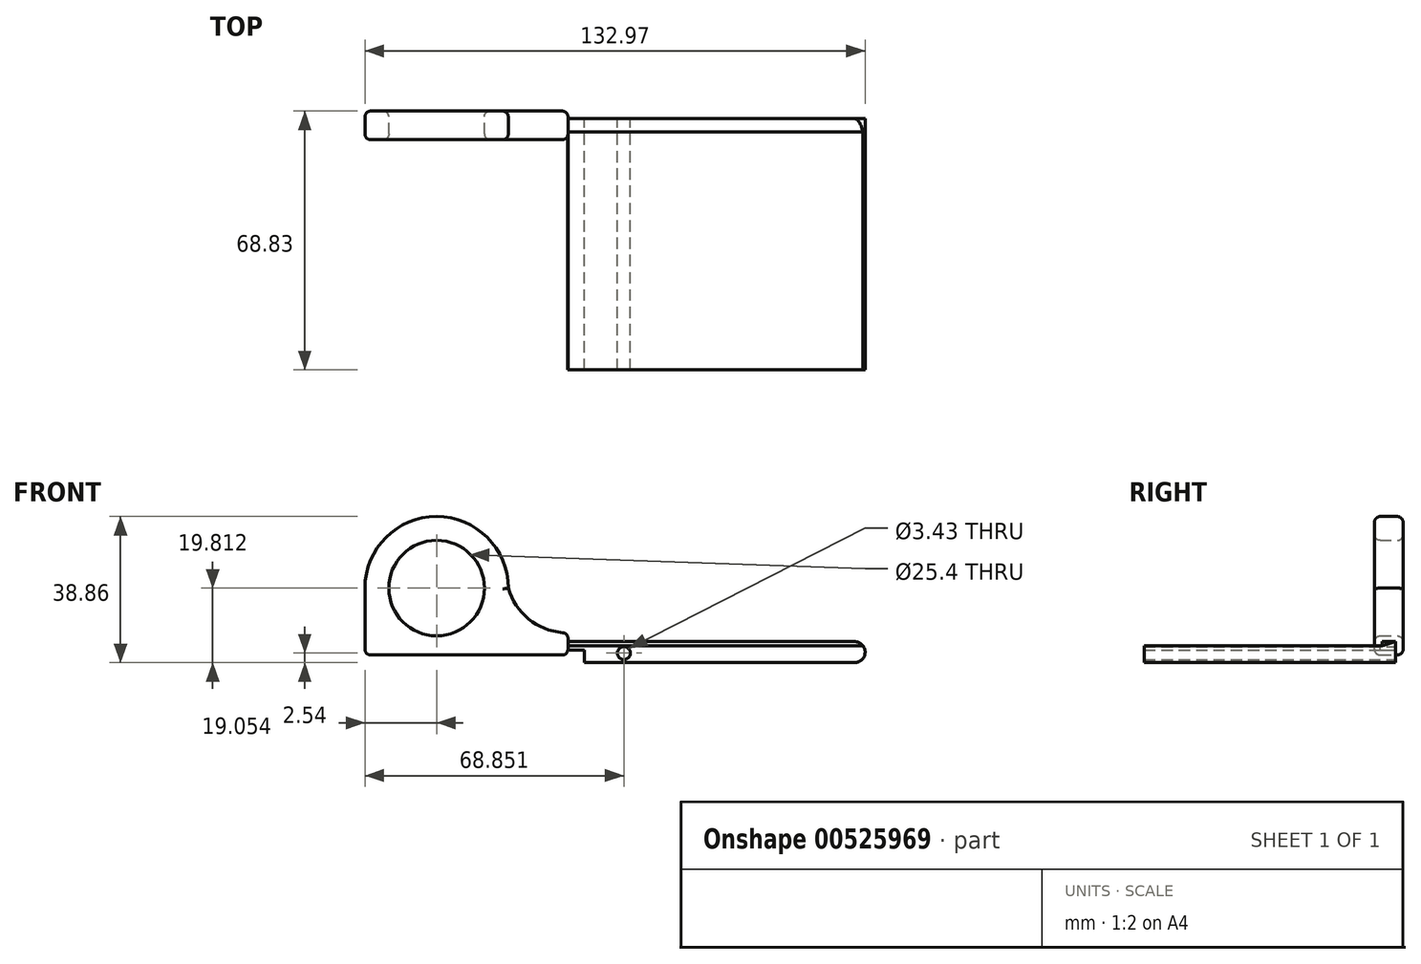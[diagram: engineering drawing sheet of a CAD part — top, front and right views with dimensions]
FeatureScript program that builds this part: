
annotation { "Feature Type Name" : "Feature", "Feature Type Description" : "" }
export const myFeature = defineFeature(function(context is Context, id is Id, definition is map)
    precondition{}
    {
        {
            var Q0;
            Q0=qCreatedBy(makeId("Front.planeOp"),FACE);
            var sketch = newSketch(context, id + "F0", { "sketchPlane" : qUnion([Q0])});
            skLineSegment(sketch, "E0", {"start": v(-53.86, -34.26) * mm, "end": v(-53.86, -16.48) * mm});
            skLineSegment(sketch, "E1", {"start": v(-53.86, -34.26) * mm, "end": v(0.12, -34.26) * mm});
            skLineSegment(sketch, "E2", {"start": v(0.12, -34.26) * mm, "end": v(0.12, -28.4) * mm});
            skLineSegment(sketch, "E3", {"start": v(0.12, -30.7) * mm, "end": v(76.32, -30.7) * mm});
            skArc(sketch, "E4", {"start": v(-15.76, -16.48) * mm, "mid": v(-34.8, 2.57) * mm, "end": v(-53.86, -16.48) * mm});
            skArc(sketch, "E5", {"start": v(-15.76, -16.48) * mm, "mid": v(-9.8, -25.09) * mm, "end": v(0.12, -28.4) * mm});
            skCircle(sketch, "E6", {"center": v(-34.8, -16.48) * mm, "radius": 12.7 * mm});
            skLineSegment(sketch, "E7", {"start": v(4.44, -32.99) * mm, "end": v(0.12, -32.99) * mm});
            skArc(sketch, "E8", {"start": v(76.32, -36.29) * mm, "mid": v(79.11, -33.5) * mm, "end": v(76.32, -30.7) * mm});
            skLineSegment(sketch, "E9", {"start": v(76.32, -36.29) * mm, "end": v(4.45, -36.29) * mm});
            skLineSegment(sketch, "E10", {"start": v(4.45, -36.29) * mm, "end": v(4.44, -32.99) * mm});
            skCircle(sketch, "E11", {"center": v(15, -33.75) * mm, "radius": 1.71 * mm});
            skSolve(sketch);
        }
        {
            var Q0;
            Q0=makeQuery(id+"F0.imprint","IMPRINT",FACE,{"disambiguationData":[TD([[makeQuery(id+"F0.imprint","IMPRINT",EDGE,{"derivedFrom":sQuery(id+"F0.wireOp",EDGE,"E0")}),-1.0]])]});
            extrude(context, id + "F1", {"entities" : qUnion([Q0]), "endBound" : BoundingType.SYMMETRIC, "depth" : 7.62 * mm});
        }
        {
            var Q0;
            {var subQ1=sQuery(id+"F0.wireOp",EDGE,"E3");Q0=makeQuery(id+"F0.imprint","IMPRINT",FACE,{"disambiguationData":[TD([[makeQuery(id+"F0.imprint","IMPRINT",EDGE,{"derivedFrom":subQ1}),-1.0]])]});}
            extrude(context, id + "F2", {"entities" : qUnion([Q0]), "operationType" : NewBodyOperationType.ADD, "endBound" : BoundingType.SYMMETRIC, "depth" : 3.56 * mm});
        }
        {
            var Q0;
            Q0=makeQuery(id+"F1.opExtrude","CAP_EDGE",EDGE,{"disambiguationData":[OSD([sQuery(id+"F0.wireOp",EDGE,"E6")])],"isStart":false});
            var Q1;
            Q1=makeQuery(id+"F1.opExtrude","CAP_EDGE",EDGE,{"disambiguationData":[OSD([sQuery(id+"F0.wireOp",EDGE,"E6")])],"isStart":true});
            var Q2;
            Q2=makeQuery(id+"F1.opExtrude","CAP_EDGE",EDGE,{"disambiguationData":[OSD([sQuery(id+"F0.wireOp",EDGE,"E0")])],"isStart":true});
            var Q3;
            Q3=makeQuery(id+"F1.opExtrude","CAP_EDGE",EDGE,{"disambiguationData":[OSD([sQuery(id+"F0.wireOp",EDGE,"E0")])],"isStart":false});
            var Q4;
            Q4=makeQuery(id+"F1.opExtrude","SWEPT_EDGE",EDGE,{"disambiguationData":[OSD([sQuery(id+"F0.wireOp",EDGE,"E0"),sQuery(id+"F0.wireOp",EDGE,"E1")])]});
            var Q5;
            Q5=makeQuery(id+"F1.opExtrude","CAP_EDGE",EDGE,{"disambiguationData":[OSD([sQuery(id+"F0.wireOp",EDGE,"E1")])],"isStart":false});
            var Q6;
            Q6=makeQuery(id+"F1.opExtrude","CAP_EDGE",EDGE,{"disambiguationData":[OSD([sQuery(id+"F0.wireOp",EDGE,"E1")])],"isStart":true});
            var Q7;
            Q7=makeQuery(id+"F1.opExtrude","CAP_EDGE",EDGE,{"disambiguationData":[OSD([sQuery(id+"F0.wireOp",EDGE,"E4")])],"isStart":false});
            var Q8;
            Q8=makeQuery(id+"F1.opExtrude","CAP_EDGE",EDGE,{"disambiguationData":[OSD([sQuery(id+"F0.wireOp",EDGE,"E4")])],"isStart":true});
            var Q9;
            Q9=makeQuery(id+"F1.opExtrude","CAP_EDGE",EDGE,{"disambiguationData":[OSD([sQuery(id+"F0.wireOp",EDGE,"E5")])],"isStart":true});
            var Q10;
            Q10=makeQuery(id+"F1.opExtrude","CAP_EDGE",EDGE,{"disambiguationData":[OSD([sQuery(id+"F0.wireOp",EDGE,"E5")])],"isStart":false});
            var Q11;
            Q11=makeQuery(id+"F1.opExtrude","CAP_EDGE",EDGE,{"disambiguationData":[OSD([sQuery(id+"F0.wireOp",EDGE,"E2")])],"isStart":false});
            var Q12;
            Q12=makeQuery(id+"F1.opExtrude","SWEPT_EDGE",EDGE,{"disambiguationData":[OSD([sQuery(id+"F0.wireOp",EDGE,"E2"),sQuery(id+"F0.wireOp",EDGE,"E5")])]});
            var Q13;
            Q13=makeQuery(id+"F1.opExtrude","CAP_EDGE",EDGE,{"disambiguationData":[OSD([sQuery(id+"F0.wireOp",EDGE,"E2")])],"isStart":true});
            var Q14;
            Q14=makeQuery(id+"F1.opExtrude","SWEPT_EDGE",EDGE,{"disambiguationData":[OSD([sQuery(id+"F0.wireOp",EDGE,"E1"),sQuery(id+"F0.wireOp",EDGE,"E2")])]});
            fillet(context, id + "F3", {"entities" : qUnion([Q0, Q1, Q2, Q3, Q4, Q5, Q6, Q7, Q8, Q9, Q10, Q11, Q12, Q13, Q14]), "radius" : 1.52 * mm, "tangentPropagation" : true, "allowEdgeOverflow" : false});
        }
        {
            var Q0;
            Q0=qCreatedBy(makeId("Right.planeOp"),FACE);
            var sketch = newSketch(context, id + "F4", { "sketchPlane" : qUnion([Q0])});
            skLineSegment(sketch, "E12", {"start": v(-1.8, -31.82) * mm, "end": v(1.82, -30.69) * mm});
            skLineSegment(sketch, "E13", {"start": v(1.82, -30.69) * mm, "end": v(-1.8, -30.69) * mm});
            skLineSegment(sketch, "E14", {"start": v(-1.8, -30.69) * mm, "end": v(-1.8, -31.82) * mm});
            skSolve(sketch);
        }
        {
            var Q0;
            Q0=makeQuery(id+"F4.imprint","IMPRINT",FACE,{"disambiguationData":[TD([[makeQuery(id+"F4.imprint","IMPRINT",EDGE,{"derivedFrom":sQuery(id+"F4.wireOp",EDGE,"E12")}),1.0]])]});
            extrude(context, id + "F5", {"entities" : qUnion([Q0]), "operationType" : NewBodyOperationType.REMOVE, "depth" : 99.57 * mm});
        }
        {
            var Q0;
            Q0=makeQuery(id+"F2.opExtrude","CAP_FACE",FACE,{"disambiguationData":[OSD([sQuery(id+"F0.wireOp",EDGE,"E2"),sQuery(id+"F0.wireOp",EDGE,"E3"),sQuery(id+"F0.wireOp",EDGE,"E7"),sQuery(id+"F0.wireOp",EDGE,"E8"),sQuery(id+"F0.wireOp",EDGE,"E9"),sQuery(id+"F0.wireOp",EDGE,"E10"),sQuery(id+"F0.wireOp",EDGE,"E11")])],"isStart":false});
            extrude(context, id + "F6", {"entities" : qUnion([Q0]), "operationType" : NewBodyOperationType.ADD, "depth" : 42.16 * mm, "offsetDistance" : 25.4 * mm});
        }
        {
            var Q0;
            Q0=makeQuery(id+"F6.opExtrude","CAP_FACE",FACE,{"disambiguationData":[OSD([sQuery(id+"F0.wireOp",EDGE,"E2"),sQuery(id+"F0.wireOp",EDGE,"E3"),sQuery(id+"F0.wireOp",EDGE,"E7"),sQuery(id+"F0.wireOp",EDGE,"E8"),sQuery(id+"F0.wireOp",EDGE,"E9"),sQuery(id+"F0.wireOp",EDGE,"E10"),sQuery(id+"F0.wireOp",EDGE,"E11")])],"isStart":false});
            extrude(context, id + "F7", {"entities" : qUnion([Q0]), "operationType" : NewBodyOperationType.REMOVE, "oppositeDirection" : true, "depth" : 41.4 * mm, "offsetDistance" : 25.4 * mm});
        }
        {
            var Q0;
            Q0=makeQuery(id+"F7.boolean.opBoolean","COPY",FACE,{"derivedFrom":makeQuery(id+"F7.opExtrude","CAP_FACE",FACE,{"disambiguationData":[OSD([sQuery(id+"F0.wireOp",EDGE,"E2"),sQuery(id+"F0.wireOp",EDGE,"E3"),sQuery(id+"F0.wireOp",EDGE,"E7"),sQuery(id+"F0.wireOp",EDGE,"E8"),sQuery(id+"F0.wireOp",EDGE,"E9"),sQuery(id+"F0.wireOp",EDGE,"E10"),sQuery(id+"F0.wireOp",EDGE,"E11")])],"isStart":false})});
            extrude(context, id + "F8", {"entities" : qUnion([Q0]), "operationType" : NewBodyOperationType.ADD, "depth" : 62.48 * mm, "offsetDistance" : 25.4 * mm});
        }
    });
